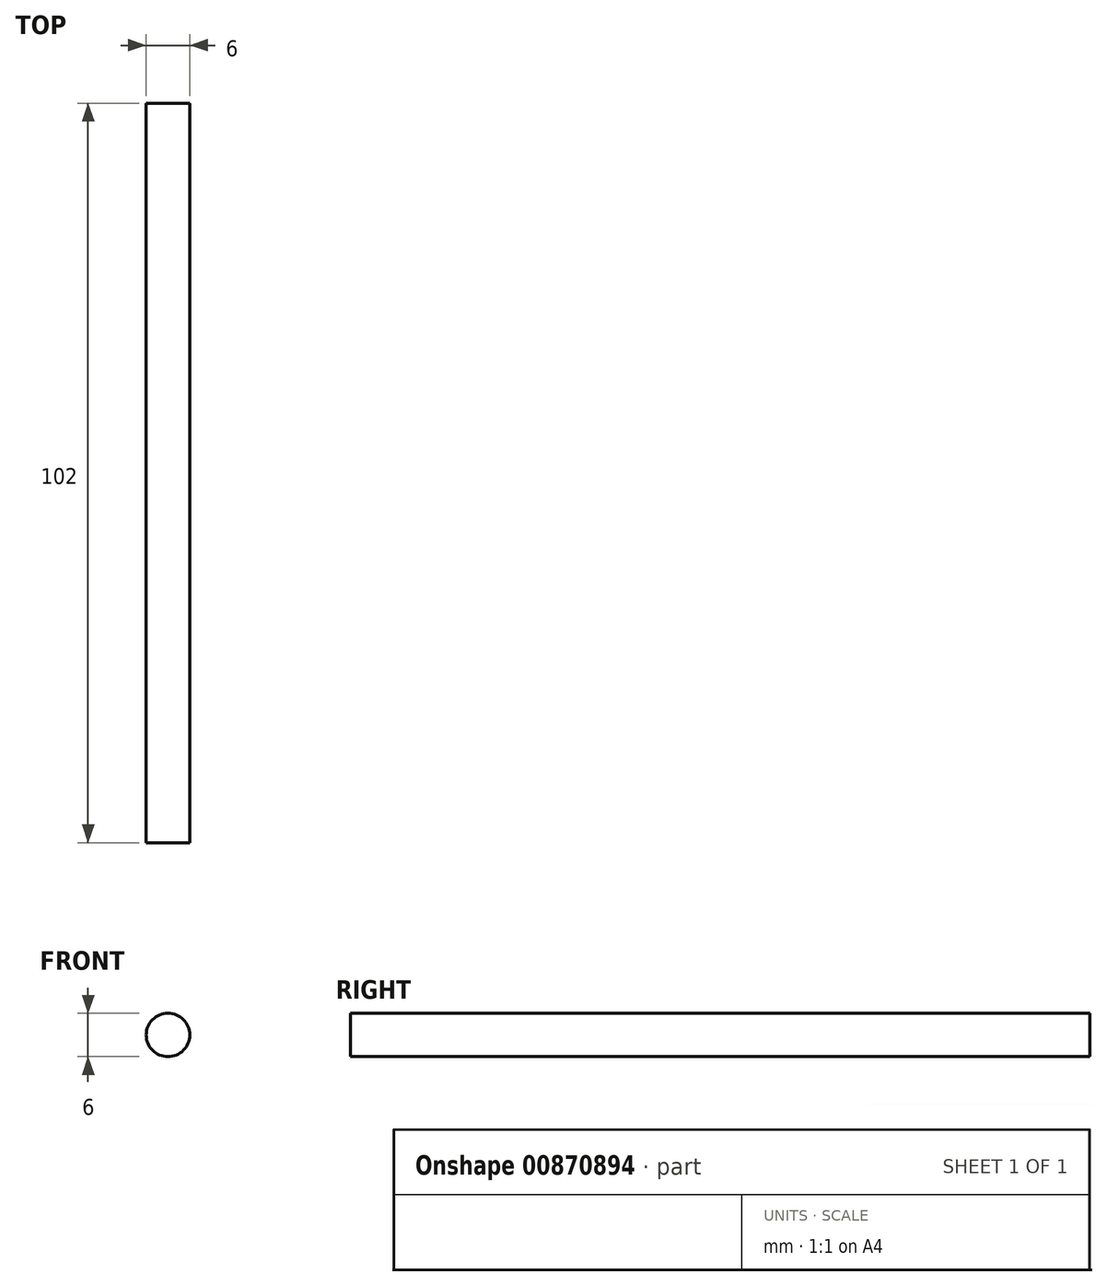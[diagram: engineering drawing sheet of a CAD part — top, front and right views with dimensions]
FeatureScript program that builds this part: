
annotation { "Feature Type Name" : "Feature", "Feature Type Description" : "" }
export const myFeature = defineFeature(function(context is Context, id is Id, definition is map)
    precondition{}
    {
        {
            var Q0;
            Q0=qCreatedBy(makeId("Front.planeOp"),FACE);
            var sketch = newSketch(context, id + "F0", { "sketchPlane" : qUnion([Q0])});
            skCircle(sketch, "E0", {"center": v(0, 0) * mm, "radius": 3 * mm});
            skSolve(sketch);
        }
        {
            var Q0;
            Q0=makeQuery(id+"F0.imprint","IMPRINT",FACE,{"disambiguationData":[TD([[makeQuery(id+"F0.imprint","IMPRINT",EDGE,{"derivedFrom":sQuery(id+"F0.wireOp",EDGE,"E0")}),1.0]])]});
            extrude(context, id + "F1", {"entities" : qUnion([Q0]), "depth" : 102 * mm, "offsetDistance" : 25 * mm});
        }
    });
